# Revit family: RN 13060 Sicherheitsgruppe
name_source: partatom
category: Rohrzubehör
units: mm (PartAtom-declared; Revit-internal decimal feet)

## family parameters
Arbeitsebenenbasiert = Nein
Beim Laden mit Abzugskörper schneiden = Nein
Bemaßung runder Anschluss = Durchmesser verwenden
Gemeinsam genutzt = Nein
Immer vertikal = Ja
Teiletyp = Ventil - Zerlegung in

## types (2) — shared parameters
1.010.00.2 Blattnummer der Richtlinie = 17
1.010.00.3 Ausgabedatum (Monat) der Richtlinie = 201601
1.010.00.4 Herstellername = R. Nussbaum AG
1.010.00.5 Revisionsdatum der Datei = 20190528
1.010.00.6 Webadresse des Herstellers = http://www.nussbaum.ch
1.100.00.3 Sortiernummer für Anzeigereihenfolge = 5
1.100.00.4 Produktbezeichnung = Sicherheitsarmaturen
1.960/3L.00.8 Link (URL) = https://www.nussbaum.ch
17.700.00.4 Armaturentyp = 6
17.700.00.6 kvs-Wert [m3/h] = 0.7
17.700.00.7 Maximale Betriebstemperatur TB [°C] = 90
17.700.00.8 Maximaler Betriebsdruck (Arbeitsdruck) ps [1.0 · 105 Pa] = 10
CONNECTOR0_dX_00 = 114 mm
CONNECTOR0_dX_01 = 104 mm
CONNECTOR0_ref_dX = 114 mm
CONNECTOR1_dX_00 = 40 mm
CONNECTOR1_dX_01 = 51 mm
CONNECTOR1_ref_dX = 51 mm
CONNECTOR2_DIAMETER_dZ_0r = 20 mm
CONNECTOR2_dZ_00 = 39 mm
CONNECTOR2_ref_dX = 16 mm
Connector Visibility = Nein
EnclosingSpace Visibility = Nein
Hersteller = R. Nussbauzm AG
URL = https://www.nussbaum.ch

## per-type parameters (varying)
| type | 1.800.00.3 TGA-Nummer | 1.810.00.3 Hersteller-Bestellnummer | 1.810.00.4 DATANORM-Nummer | 1.810.00.5 StLB-Nummer | 1.810.00.6 GTIN-Nummer | 17.700.00.30 Produktbeschreibung | 17.700.00.5 Nennweite DN | CONNECTOR0_DIAMETER_dX_0r | CONNECTOR1_DIAMETER_dX_0r | CONNECTOR2_dZ_01 | CONNECTOR2_ref_dZ | Modell | R. Nussbaum AG 13060.34 de Visibility | R. Nussbaum AG 13060.35 de Visibility | Typenkommentare |
| DN 15 | 00500700000000000000000000000200700000000000000001???00000 | 13060.34 | 13060.34 | 612.213 | 7612945044853 | 13060.34, Sicherheitsgruppe, ohne Verschraubungen, mit DRV, DN=15, Rp=¾ | 15 | 15 mm | 15 mm | 24 mm | 24 mm | 13060.34 | Ja | Nein | SicherheitsgruppeDN 15 |
| DN 20 | 00500700000000000000000000000200700000000000000002???00000 | 13060.35 | 13060.35 | 612.214 | 7612945044860 | 13060.35, Sicherheitsgruppe, ohne Verschraubungen, mit DRV, DN=20, Rp=1 | 20 | 20 mm | 20 mm | 22 mm  [stored 0.0721785 ft] | 22 mm  [stored 0.0721785 ft] | 13060.35 | Nein | Ja | SicherheitsgruppeDN 20 |

note: [stored X ft] marks values corroborated as IEEE doubles in the binary element streams (Revit-internal decimal feet)

## geometry (parser evidence)
native form markers: Sweep x1
no freeform markers — native parametric forms only
